# Revit family: Window-Casement-Pella-Architect-Contemporary-Transom-2
name_source: partatom
category: Windows
revit_build: Autodesk Revit Architecture 2013 (Build: 20130531_2115(x64)
units: mm (PartAtom-declared; Revit-internal decimal feet)

## types (1)
- Default Load Type Catalog
    Analytic Construction = <None>
    Assembly Code = B2020130
    Cladding = Aluminum
    Default Sill Height = 3' - 0"
    Depth = 0' - 5"
    Description = Aluminum Clad Wood Window
    Energy Star = http://www.pella.com
    Finish = Aluminum-Pella-EnduraClad-White
    Glass Thickness = 0' - 0 11/16"
    Glazing = Glass-Pella-Low_E-Argon
    Grille Height = 2' - 0 9/32"
    Grille Width = 1' - 7 9/32"
    Heat Transfer Coefficient (U) = 0.1 BTU/(h·ft²·°F)
    Height = 2' - 5"
    Horizontal Grille Offset = 0' - 8 3/32"
    Horizontal Grille Spacing = 0' - 8 3/32"
    Horizontal Mullions = 2
    Inset = 0' - 0"
    Interior Finish = Wood-Pella-Pine
    Jamb Extensions = Yes
    LEED = http://professional.pella.com
    Manufacturer = Pella
    Material = Wood - Pine
    Max Height = 2' - 5"
    Max Lites = 10
    Max Width = 2' - 11"
    Min Height = 1' - 2"
    Min Width = 1' - 5"
    Model = Casement Transom
    Mullions = 0' - 0 7/8"
    Nail Fin = Yes
    Offset = 0' - 0"
    Operation = Fixed
    Prairie Grille = No
    Prairie Offset = 0' - 3"
    Product Documentation Link = http://media.pella.com
    Product Name = Architect Series Contemporary
    Product Page URL = http://professional.pella.com
    Requested Height = 2' - 5"
    Requested Width = 2' - 0"
    Rough Height = 2' - 5 3/4"
    Rough Width = 2' - 0 3/4"
    Solar Heat Gain Coefficient = 0
    Specification = http://media.pella.com
    Thermal Resistance (R) = 10.0000 (h·ft²·°F)/BTU
    Traditional Grille = No
    Traditional Grille Array Horizontal = No
    Traditional Grille Array Vertical = No
    Traditional Grille Single Horizontal = No
    Traditional Grille Single Vertical = No
    Traditional Lites High = 2
    Traditional Lites Wide = 2
    Type Comments = Casement
    URL = http://professional.pella.com
    Vertical Grille Offset = 0' - 6 7/16"
    Vertical Grille Spacing = 0' - 6 7/16"
    Vertical Mullions = 2
    Visual Light Transmittance = 0
    Wall Closure = By host
    Warranty = https://content.pella.com
    Width = 2' - 0"

## geometry (parser evidence)
native form markers: Blend x29, Sweep x7
no freeform markers — native parametric forms only
